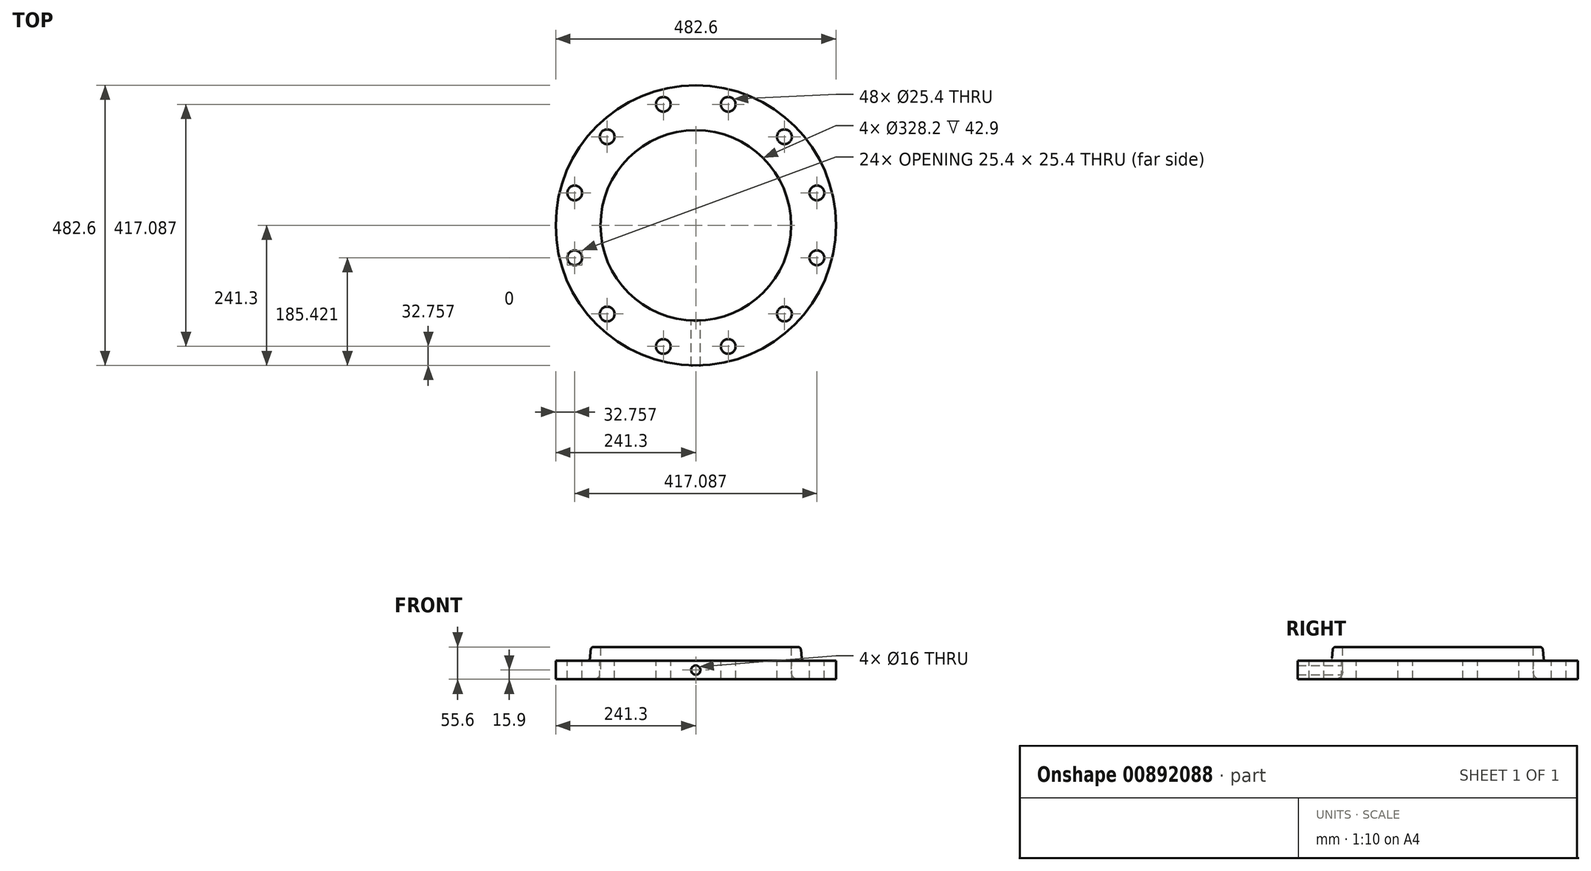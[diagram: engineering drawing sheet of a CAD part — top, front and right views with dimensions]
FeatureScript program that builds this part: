
annotation { "Feature Type Name" : "Feature", "Feature Type Description" : "" }
export const myFeature = defineFeature(function(context is Context, id is Id, definition is map)
    precondition{}
    {
        {
            var Q0;
            Q0=qCreatedBy(makeId("Front.planeOp"),FACE);
            var sketch = newSketch(context, id + "F0", { "sketchPlane" : qUnion([Q0])});
            skLineSegment(sketch, "E0", {"start": v(176.8, 0) * mm, "end": v(241.3, 0) * mm});
            skLineSegment(sketch, "E1", {"start": v(241.3, 0) * mm, "end": v(241.3, 31.8) * mm});
            skLineSegment(sketch, "E2", {"start": v(241.3, 31.8) * mm, "end": v(187.23, 31.8) * mm});
            skLineSegment(sketch, "E3", {"start": v(182.25, 36.36) * mm, "end": v(180.97, 51.04) * mm});
            skLineSegment(sketch, "E4", {"start": v(175.99, 55.6) * mm, "end": v(164.1, 55.6) * mm});
            skLineSegment(sketch, "E5", {"start": v(164.1, 55.6) * mm, "end": v(164.1, 12.7) * mm});
            skLineSegment(sketch, "E6", {"start": v(0, 0) * mm, "end": v(0, 55.6) * mm});
            skPoint(sketch, "E7.visualSharp", {"position": v(164.1, 0) * mm});
            skArc(sketch, "E7.filletArc", {"start": v(164.1, 12.7) * mm, "mid": v(167.82, 3.72) * mm, "end": v(176.8, 0) * mm});
            skPoint(sketch, "E8.visualSharp", {"position": v(180.57, 55.6) * mm});
            skArc(sketch, "E8.filletArc", {"start": v(180.97, 51.04) * mm, "mid": v(179.36, 54.29) * mm, "end": v(175.99, 55.6) * mm});
            skPoint(sketch, "E9.visualSharp", {"position": v(182.65, 31.8) * mm});
            skArc(sketch, "E9.filletArc", {"start": v(182.25, 36.36) * mm, "mid": v(183.85, 33.11) * mm, "end": v(187.23, 31.8) * mm});
            skSolve(sketch);
        }
        {
            var Q0;
            Q0=makeQuery(id+"F0.imprint","IMPRINT",FACE,{"disambiguationData":[TD([[makeQuery(id+"F0.imprint","IMPRINT",EDGE,{"derivedFrom":sQuery(id+"F0.wireOp",EDGE,"newPmkzC-CrfG-sXBi-HGfB-OUHVhpxAI036")}),1.0]])]});
            var Q1;
            Q1=makeQuery(id+"F0.imprint","IMPRINT",FACE,{"disambiguationData":[TD([[makeQuery(id+"F0.imprint","IMPRINT",EDGE,{"derivedFrom":sQuery(id+"F0.wireOp",EDGE,"E0")}),1.0]])]});
            var Q2;
            Q2=sQuery(id+"F0.wireOp",EDGE,"E6");
            revolve(context, id + "F1", {"surfaceOperationType" : NewSurfaceOperationType.NEW, "entities" : qUnion([Q0, Q1]), "axis" : qUnion([Q2]), "revolveType" : RevolveType.FULL});
        }
        {
            var Q0;
            Q0=makeQuery(id+"F1.opRevolve","SWEPT_FACE",FACE,{"disambiguationData":[OSD([sQuery(id+"F0.wireOp",EDGE,"E2")])]});
            var sketch = newSketch(context, id + "F2", { "sketchPlane" : qUnion([Q0])});
            skCircle(sketch, "E10", {"center": v(0, 0) * mm, "radius": 215.9 * mm, "construction": true});
            skCircle(sketch, "E11", {"center": v(-55.88, 208.54) * mm, "radius": 12.7 * mm});
            skCircle(sketch, "E12.1.0", {"center": v(-152.66, 152.66) * mm, "radius": 12.7 * mm});
            skCircle(sketch, "E12.2.0", {"center": v(-208.54, 55.88) * mm, "radius": 12.7 * mm});
            skCircle(sketch, "E12.3.0", {"center": v(-208.54, -55.88) * mm, "radius": 12.7 * mm});
            skCircle(sketch, "E12.4.0", {"center": v(-152.66, -152.66) * mm, "radius": 12.7 * mm});
            skCircle(sketch, "E12.5.0", {"center": v(-55.88, -208.54) * mm, "radius": 12.7 * mm});
            skCircle(sketch, "E12.6.0", {"center": v(55.88, -208.54) * mm, "radius": 12.7 * mm});
            skCircle(sketch, "E12.7.0", {"center": v(152.66, -152.66) * mm, "radius": 12.7 * mm});
            skCircle(sketch, "E12.8.0", {"center": v(208.54, -55.88) * mm, "radius": 12.7 * mm});
            skCircle(sketch, "E12.9.0", {"center": v(208.54, 55.88) * mm, "radius": 12.7 * mm});
            skCircle(sketch, "E12.10.0", {"center": v(152.66, 152.66) * mm, "radius": 12.7 * mm});
            skCircle(sketch, "E12.11.0", {"center": v(55.88, 208.54) * mm, "radius": 12.7 * mm});
            skLineSegment(sketch, "E13", {"start": v(-55.88, 208.54) * mm, "end": v(55.88, 208.54) * mm, "construction": true});
            skSolve(sketch);
        }
        {
            var Q0;
            Q0=qSketchRegion(id+"F2",true);
            extrude(context, id + "F3", {"entities" : qUnion([Q0]), "operationType" : NewBodyOperationType.REMOVE, "endBound" : BoundingType.THROUGH_ALL, "oppositeDirection" : true, "depth" : 25 * mm, "offsetDistance" : 25 * mm});
        }
        {
            var Q0;
            Q0=qCreatedBy(makeId("Front.planeOp"),FACE);
            var sketch = newSketch(context, id + "F4", { "sketchPlane" : qUnion([Q0])});
            skCircle(sketch, "E14", {"center": v(0, 15.9) * mm, "radius": 8 * mm});
            skSolve(sketch);
        }
        {
            var Q0;
            Q0=makeQuery(id+"F4.imprint","IMPRINT",FACE,{"disambiguationData":[TD([[makeQuery(id+"F4.imprint","IMPRINT",EDGE,{"derivedFrom":sQuery(id+"F4.wireOp",EDGE,"E14")}),1.0]])]});
            extrude(context, id + "F5", {"entities" : qUnion([Q0]), "operationType" : NewBodyOperationType.REMOVE, "endBound" : BoundingType.THROUGH_ALL, "depth" : 25 * mm, "offsetDistance" : 25 * mm});
        }
    });
